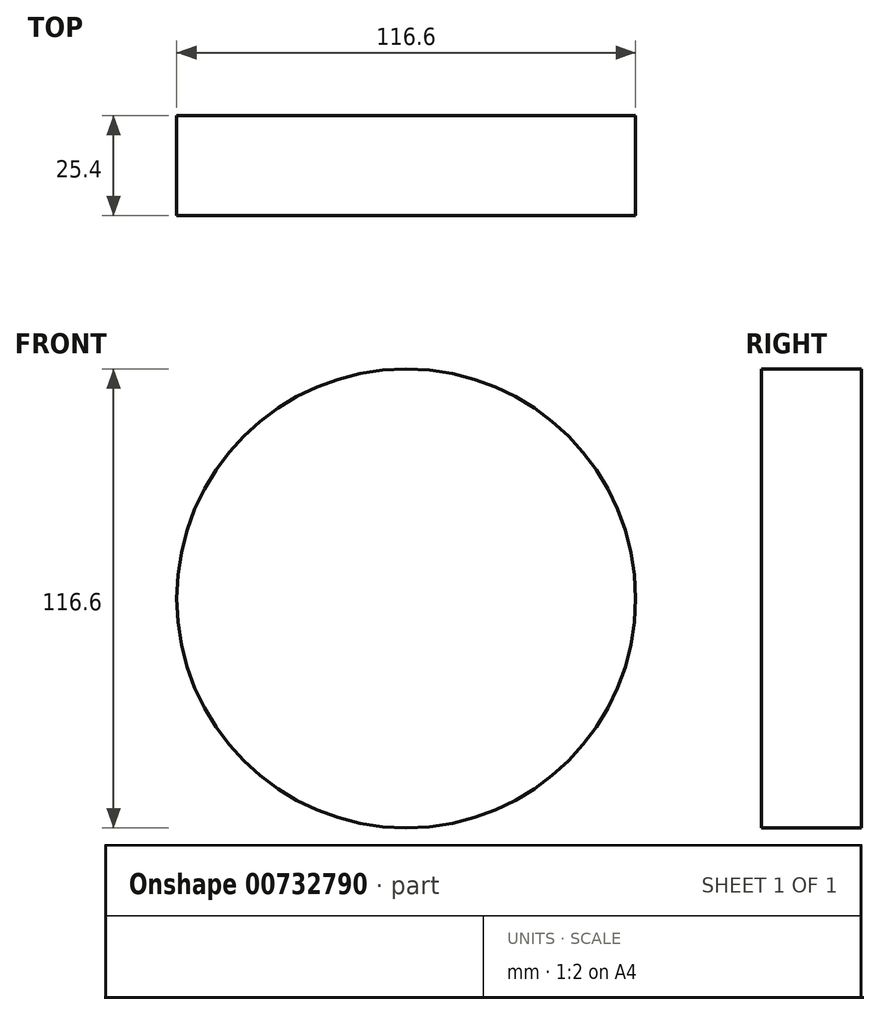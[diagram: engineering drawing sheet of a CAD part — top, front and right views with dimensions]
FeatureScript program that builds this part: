
annotation { "Feature Type Name" : "Feature", "Feature Type Description" : "" }
export const myFeature = defineFeature(function(context is Context, id is Id, definition is map)
    precondition{}
    {
        {
            var Q0;
            Q0=qCreatedBy(makeId("Front.planeOp"),FACE);
            var sketch = newSketch(context, id + "F0", { "sketchPlane" : qUnion([Q0])});
            skCircle(sketch, "E0", {"center": v(0, 0) * mm, "radius": 58.3 * mm});
            skSolve(sketch);
        }
        {
            var Q0;
            Q0=makeQuery(id+"F0.imprint","IMPRINT",FACE,{"disambiguationData":[TD([[makeQuery(id+"F0.imprint","IMPRINT",EDGE,{"derivedFrom":sQuery(id+"F0.wireOp",EDGE,"E0")}),1.0]])]});
            extrude(context, id + "F1", {"entities" : qUnion([Q0]), "depth" : 25.4 * mm, "offsetDistance" : 25.4 * mm});
        }
        {
            var Q0;
            Q0=makeQuery(id+"F1.opExtrude","CAP_FACE",FACE,{"disambiguationData":[OSD([sQuery(id+"F0.wireOp",EDGE,"E0")])],"isStart":false});
            var sketch = newSketch(context, id + "F2", { "sketchPlane" : qUnion([Q0])});
            skSolve(sketch);
        }
        {
            var Q0;
            Q0=makeQuery(id+"F2.imprint","IMPRINT",FACE,{"disambiguationData":[TD([[makeQuery(id+"F2.imprint","IMPRINT",EDGE,{"derivedFrom":makeQuery(id+"F1.opExtrude","CAP_EDGE",EDGE,{"disambiguationData":[OSD([sQuery(id+"F0.wireOp",EDGE,"E0")])],"isStart":false})}),1.0]])]});
            var sketch = newSketch(context, id + "F3", { "sketchPlane" : qUnion([Q0])});
            skCircle(sketch, "E1", {"center": v(0, 0) * mm, "radius": 8.22 * mm});
            skSolve(sketch);
        }
        {
            var Q0;
            Q0=sQuery(id+"F3.wireOp",EDGE,"E1");
            extrude(context, id + "F4", {"bodyType" : ToolBodyType.SURFACE, "surfaceEntities" : qUnion([Q0]), "oppositeDirection" : true, "depth" : 25.4 * mm, "offsetDistance" : 25.4 * mm});
        }
        {
            var Q0;
            Q0=makeQuery(id+"F1.opExtrude","SWEPT_BODY",BODY,{"disambiguationData":[OSD([sQuery(id+"F0.wireOp",EDGE,"E0")])]});
            var Q1;
            Q1=qCreatedBy(makeId("Top.planeOp"),FACE);
            mirror(context, id + "F5", {"operationType" : NewBodyOperationType.ADD, "entities" : qUnion([Q0]), "mirrorPlane" : qUnion([Q1])});
        }
    });
